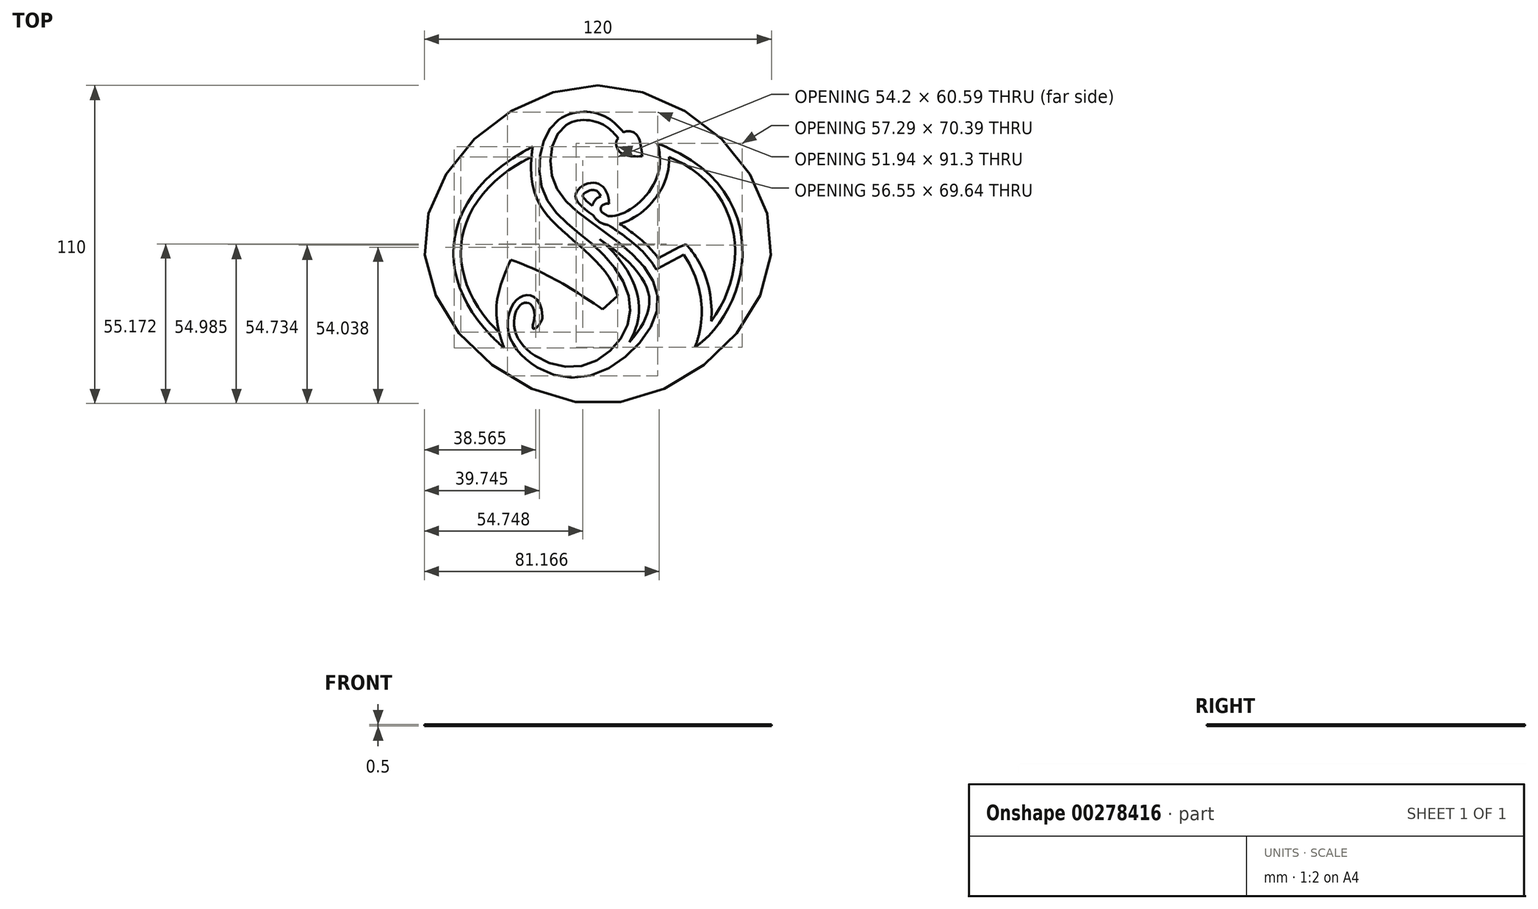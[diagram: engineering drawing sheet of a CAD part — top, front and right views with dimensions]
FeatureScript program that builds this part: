
annotation { "Feature Type Name" : "Feature", "Feature Type Description" : "" }
export const myFeature = defineFeature(function(context is Context, id is Id, definition is map)
    precondition{}
    {
        {
            var Q0;
            Q0=qCreatedBy(makeId("Top.planeOp"),FACE);
            var sketch = newSketch(context, id + "F0", { "sketchPlane" : qUnion([Q0])});
            skPoint(sketch, "E0", {"position": v(0, 45.9) * mm});
            skPoint(sketch, "E1", {"position": v(50, 0) * mm});
            skFitSpline(sketch, "E2", {"points": [v(-32.4, -35.78) * mm, v(-22.5, 33.86) * mm], "startDerivative": vector(-72.76, 61.38) * mm, "endDerivative": vector(106.5, 54.47) * mm});
            skFitSpline(sketch, "E3", {"points": [v(-22.5, 33.86) * mm, v(-11.83, 4.4) * mm, v(6.84, -17.73) * mm], "startDerivative": vector(-15.53, -95.65) * mm, "endDerivative": vector(14.34, -53.92) * mm});
            skFitSpline(sketch, "E4", {"points": [v(-32.4, -35.78) * mm, v(-30.16, -5.24) * mm], "startDerivative": vector(-15.68, 40.02) * mm, "endDerivative": vector(13, 31.32) * mm});
            skFitSpline(sketch, "E5", {"points": [v(-30.16, -5.24) * mm, v(1.65, -22.42) * mm], "startDerivative": vector(35.17, -12.5) * mm, "endDerivative": vector(34.2, -23.48) * mm});
            skLineSegment(sketch, "E6", {"start": v(1.65, -22.42) * mm, "end": v(6.84, -17.73) * mm});
            skFitSpline(sketch, "E7", {"points": [v(20.58, 34.93) * mm, v(33.56, -35.46) * mm], "startDerivative": vector(125.66, -46.66) * mm, "endDerivative": vector(-57.33, -38.36) * mm});
            skFitSpline(sketch, "E8", {"points": [v(33.56, -35.46) * mm, v(29.63, -3.46) * mm], "startDerivative": vector(13.37, 33.93) * mm, "endDerivative": vector(-18.4, 26.9) * mm});
            skFitSpline(sketch, "E9", {"points": [v(20.58, 34.93) * mm, v(2.5, 10.15) * mm, v(3.85, 14.15) * mm], "startDerivative": vector(20.7, -63.95) * mm, "endDerivative": vector(42.66, -0.52) * mm});
            skFitSpline(sketch, "E10", {"points": [v(29.63, -3.46) * mm, v(20.13, -8.6) * mm], "startDerivative": vector(-9.5, -5.15) * mm, "endDerivative": vector(-9.5, -5.15) * mm});
            skFitSpline(sketch, "E11", {"points": [v(3.85, 14.15) * mm, v(-2.2, 21.34) * mm, v(-7.68, 16.17) * mm, v(20.13, -8.6) * mm], "startDerivative": vector(-2.08, 58.94) * mm, "endDerivative": vector(39.46, -73.33) * mm});
            skFitSpline(sketch, "E12", {"points": [v(-19.17, -24.83) * mm, v(-26.46, -18) * mm, v(-30.6, -31.45) * mm, v(-5.87, -45.9) * mm, v(20.63, -21.21) * mm, v(5.08, 2.3) * mm, v(-15.3, 21.72) * mm, v(-11.54, 40.91) * mm, v(2, 41.36) * mm, v(7.04, 36.8) * mm], "startDerivative": vector(-12.75, 250.76) * mm, "endDerivative": vector(40.26, -40.75) * mm});
            skFitSpline(sketch, "E13", {"points": [v(-22.04, -25.78) * mm, v(-25.84, -20.3) * mm, v(-28.42, -30.72) * mm, v(-7.28, -42.28) * mm, v(10.94, -25.14) * mm, v(0.7, -2.29) * mm, v(-18.36, 17) * mm, v(-16.38, 40.34) * mm, v(-4.35, 45.9) * mm, v(4.17, 43.23) * mm, v(8.8, 38.82) * mm], "startDerivative": vector(32.24, 214.47) * mm, "endDerivative": vector(67.48, -74.16) * mm});
            skFitSpline(sketch, "E14", {"points": [v(-22.04, -25.78) * mm, v(-22.22, -29.13) * mm, v(-19.17, -24.83) * mm], "startDerivative": vector(-3.03, -14.05) * mm, "endDerivative": vector(1.13, 14.14) * mm});
            skFitSpline(sketch, "E15", {"points": [v(7.04, 36.8) * mm, v(6.52, 33.67) * mm, v(8.55, 31.33) * mm, v(15.3, 30.52) * mm], "startDerivative": vector(-8.7, -10.3) * mm, "endDerivative": vector(19.55, 1.32) * mm});
            skFitSpline(sketch, "E16", {"points": [v(8.8, 38.82) * mm, v(11.3, 39.15) * mm, v(13.78, 37.37) * mm, v(15.3, 30.52) * mm], "startDerivative": vector(7.23, 3.73) * mm, "endDerivative": vector(1.32, -17.53) * mm});
            skFitSpline(sketch, "E17", {"points": [v(0, 55) * mm, v(60, 0) * mm, v(0, -55) * mm, v(-60, 0) * mm, v(0, 55) * mm]});
            skFitSpline(sketch, "E18.0", {"points": [v(23.43, 35.85) * mm, v(23.93, 34.32) * mm, v(24.55, 31.27) * mm, v(24.48, 26.9) * mm, v(23.54, 22.83) * mm, v(21.92, 19.15) * mm, v(19.8, 15.9) * mm, v(17.3, 13.09) * mm, v(14.57, 10.74) * mm, v(11.72, 8.88) * mm, v(9.32, 7.76) * mm, v(7.42, 7.15) * mm, v(5.99, 6.85) * mm, v(4.56, 6.72) * mm, v(3.36, 6.8) * mm, v(2.4, 7) * mm, v(1.67, 7.23) * mm, v(0.96, 7.55) * mm, v(0.31, 7.96) * mm, v(-0.27, 8.44) * mm, v(-0.96, 9.15) * mm, v(-1.64, 10.2) * mm, v(-2.03, 11.48) * mm, v(-2.07, 12.62) * mm, v(-1.94, 13.52) * mm, v(-1.6, 14.4) * mm, v(-1.07, 15.21) * mm, v(-0.4, 15.9) * mm, v(0.38, 16.4) * mm, v(1.21, 16.77) * mm, v(2.36, 17.09) * mm, v(3.26, 17.16) * mm, v(3.88, 17.15) * mm]});
            skLineSegment(sketch, "E19.0", {"start": v(-0.36, -20.2) * mm, "end": v(3.39, -16.81) * mm});
            skFitSpline(sketch, "E19.1", {"points": [v(-25.47, 34.34) * mm, v(-25.81, 32.25) * mm, v(-26.23, 28.34) * mm, v(-26.14, 23.16) * mm, v(-25.36, 18.58) * mm, v(-23.96, 14.54) * mm, v(-22.02, 11) * mm, v(-19.68, 7.9) * mm, v(-17.07, 5.13) * mm, v(-14.75, 2.98) * mm, v(-12.85, 1.3) * mm, v(-10.91, -0.4) * mm, v(-8.48, -2.5) * mm, v(-5.63, -5.06) * mm, v(-2.95, -7.66) * mm, v(-0.56, -10.3) * mm, v(1.46, -13) * mm, v(3, -15.73) * mm, v(3.7, -17.57) * mm, v(3.94, -18.5) * mm]});
            skFitSpline(sketch, "E19.2", {"points": [v(-30.47, -33.49) * mm, v(-33.36, -31.05) * mm, v(-38.44, -25.87) * mm, v(-43.78, -17.54) * mm, v(-46.75, -8.95) * mm, v(-47.3, -0.33) * mm, v(-45.3, 8.16) * mm, v(-40.58, 16.43) * mm, v(-32.8, 24.26) * mm, v(-25.42, 29) * mm, v(-21.14, 31.19) * mm]});
            skFitSpline(sketch, "E19.3", {"points": [v(-35.2, -36.88) * mm, v(-35.88, -35.12) * mm, v(-37, -31.8) * mm, v(-37.95, -27.21) * mm, v(-38.23, -22.95) * mm, v(-37.91, -18.96) * mm, v(-37.1, -15.18) * mm, v(-35.55, -10.32) * mm, v(-34, -6.7) * mm, v(-32.93, -4.1) * mm]});
            skFitSpline(sketch, "E20.0", {"points": [v(-29.15, -2.42) * mm, v(-26.15, -3.48) * mm, v(-20.5, -5.76) * mm, v(-12.66, -9.72) * mm, v(-4.93, -14.36) * mm, v(0.48, -17.98) * mm, v(3.35, -19.95) * mm]});
            skLineSegment(sketch, "E21", {"start": v(-32.93, -4.1) * mm, "end": v(-31.1, -1.34) * mm});
            skLineSegment(sketch, "E22", {"start": v(-29.15, -2.42) * mm, "end": v(-31.6, -2.08) * mm});
            skPoint(sketch, "E23", {"position": v(-2.05, 12.14) * mm});
            skPoint(sketch, "E24", {"position": v(5.67, 6.84) * mm});
            skPoint(sketch, "E25", {"position": v(1.33, 16.8) * mm});
            skPoint(sketch, "E26", {"position": v(24.33, 31.77) * mm});
            skPoint(sketch, "E27", {"position": v(21.18, 32.56) * mm});
            skPoint(sketch, "E28", {"position": v(1.4, -18.61) * mm});
            skFitSpline(sketch, "E29.0", {"points": [v(19.54, 32.12) * mm, v(24.55, 30.26) * mm, v(32.92, 25.78) * mm, v(41.15, 17.55) * mm, v(45.8, 8.34) * mm, v(47.39, -1.4) * mm, v(46.34, -11.11) * mm, v(43.09, -20.16) * mm, v(38.1, -27.82) * mm, v(34.02, -31.55) * mm, v(31.9, -32.97) * mm]});
            skFitSpline(sketch, "E30.0", {"points": [v(36.36, -36.56) * mm, v(37.57, -33.49) * mm, v(39.08, -27.26) * mm, v(38.9, -18.08) * mm, v(36.56, -9.41) * mm, v(33.76, -4.2) * mm, v(32.1, -1.77) * mm]});
            skFitSpline(sketch, "E31.0", {"points": [v(28.2, -0.82) * mm, v(25.03, -2.54) * mm, v(21.87, -4.26) * mm, v(18.7, -5.97) * mm]});
            skFitSpline(sketch, "E32.0", {"points": [v(1.35, 14.06) * mm, v(1.31, 15.08) * mm, v(1.08, 16.33) * mm, v(0.57, 17.44) * mm, v(0.15, 18.03) * mm, v(-0.29, 18.43) * mm, v(-0.74, 18.68) * mm, v(-1.24, 18.83) * mm, v(-1.73, 18.87) * mm, v(-2.16, 18.83) * mm, v(-2.65, 18.74) * mm, v(-3.3, 18.54) * mm, v(-4.04, 18.16) * mm, v(-4.65, 17.7) * mm, v(-5.06, 17.24) * mm, v(-5.2, 16.95) * mm, v(-5.24, 16.82) * mm, v(-5.25, 16.76) * mm, v(-5.24, 16.73) * mm, v(-5.24, 16.69) * mm, v(-5.21, 16.61) * mm, v(-5.14, 16.45) * mm, v(-4.9, 16.07) * mm, v(-4.34, 15.4) * mm, v(-3.26, 14.43) * mm, v(-1.86, 13.35) * mm, v(-0.18, 12.18) * mm, v(2.35, 10.5) * mm, v(5.93, 8.2) * mm, v(10.51, 5.09) * mm, v(15.04, 1.53) * mm, v(19.18, -2.56) * mm, v(21.42, -5.72) * mm, v(22.34, -7.43) * mm]});
            skLineSegment(sketch, "E33", {"start": v(28.2, -0.82) * mm, "end": v(30.38, 0) * mm});
            skLineSegment(sketch, "E34", {"start": v(30.38, 0) * mm, "end": v(32.1, -1.77) * mm});
            skFitSpline(sketch, "E35.0", {"points": [v(-22.16, -24.98) * mm, v(-22.22, -23.9) * mm, v(-22.47, -22.62) * mm, v(-22.93, -21.57) * mm, v(-23.28, -21.06) * mm, v(-23.59, -20.76) * mm, v(-23.85, -20.6) * mm, v(-24.1, -20.52) * mm, v(-24.37, -20.5) * mm, v(-24.7, -20.53) * mm, v(-25.08, -20.64) * mm, v(-25.48, -20.86) * mm, v(-25.94, -21.2) * mm, v(-26.4, -21.7) * mm, v(-27, -22.52) * mm, v(-27.67, -23.85) * mm, v(-28.17, -25.8) * mm, v(-28.27, -27.6) * mm, v(-28.11, -29.07) * mm, v(-27.87, -30.17) * mm, v(-27.5, -31.27) * mm, v(-27, -32.4) * mm, v(-26.35, -33.53) * mm, v(-25.3, -35.02) * mm, v(-23.67, -36.84) * mm, v(-21.27, -38.83) * mm, v(-18.52, -40.53) * mm, v(-15.49, -41.86) * mm, v(-12.8, -42.6) * mm, v(-10.62, -42.94) * mm, v(-8.95, -43.06) * mm, v(-7.28, -43.03) * mm, v(-5.62, -42.86) * mm, v(-3.93, -42.54) * mm, v(-1.65, -41.9) * mm, v(1.2, -40.77) * mm, v(4.52, -38.9) * mm, v(7.66, -36.61) * mm, v(10.53, -34) * mm, v(13.02, -31.16) * mm, v(15.07, -28.19) * mm, v(16.33, -25.7) * mm, v(17.05, -23.76) * mm, v(17.43, -22.35) * mm, v(17.62, -21.23) * mm, v(17.7, -20.36) * mm, v(17.75, -19.07) * mm, v(17.55, -17.2) * mm, v(16.78, -14.7) * mm, v(15.5, -12.21) * mm, v(13.2, -8.9) * mm, v(9.32, -4.86) * mm, v(4.63, -1.06) * mm, v(0.73, 1.8) * mm, v(-3.21, 4.6) * mm, v(-7.09, 7.4) * mm, v(-10.68, 10.4) * mm, v(-13.16, 12.82) * mm, v(-15, 15.02) * mm, v(-16.28, 16.92) * mm, v(-17.14, 18.42) * mm, v(-17.88, 20.01) * mm, v(-18.48, 21.68) * mm, v(-18.93, 23.39) * mm, v(-19.35, 25.7) * mm, v(-19.55, 28.64) * mm, v(-19.28, 32.13) * mm, v(-18.51, 35.48) * mm, v(-17.47, 38.08) * mm, v(-16.36, 40) * mm, v(-15.4, 41.33) * mm, v(-14.46, 42.34) * mm, v(-13.64, 43.08) * mm, v(-12.76, 43.76) * mm, v(-11.61, 44.47) * mm, v(-9.67, 45.34) * mm, v(-7.16, 45.97) * mm, v(-4.14, 46.11) * mm, v(-1.71, 45.81) * mm, v(0.14, 45.35) * mm, v(1.48, 44.9) * mm, v(2.75, 44.36) * mm, v(3.95, 43.71) * mm, v(5.01, 43) * mm, v(6.27, 42.02) * mm, v(7.28, 41.03) * mm, v(8.08, 40.16) * mm, v(8.58, 39.59) * mm, v(8.96, 39.14) * mm, v(9.13, 38.96) * mm, v(9.17, 38.92) * mm]});
            skFitSpline(sketch, "E36.0", {"points": [v(-19.07, -26.23) * mm, v(-18.96, -25.53) * mm, v(-18.86, -24.2) * mm, v(-19.04, -22.34) * mm, v(-19.57, -20.64) * mm, v(-20.48, -19.15) * mm, v(-21.75, -17.98) * mm, v(-23.3, -17.26) * mm, v(-24.95, -17.04) * mm, v(-26.3, -17.26) * mm, v(-27.3, -17.65) * mm, v(-28.2, -18.16) * mm, v(-29.17, -18.95) * mm, v(-30.09, -20.07) * mm, v(-30.82, -21.31) * mm, v(-31.38, -22.66) * mm, v(-31.92, -24.58) * mm, v(-32.13, -26.66) * mm, v(-31.98, -28.83) * mm, v(-31.72, -30.22) * mm, v(-31.4, -31.32) * mm, v(-31, -32.43) * mm, v(-30.37, -33.75) * mm, v(-29.44, -35.26) * mm, v(-27.99, -37.15) * mm, v(-25.82, -39.3) * mm, v(-22.77, -41.49) * mm, v(-19.37, -43.27) * mm, v(-15.7, -44.59) * mm, v(-12.49, -45.22) * mm, v(-9.87, -45.4) * mm, v(-7.9, -45.38) * mm, v(-5.91, -45.16) * mm, v(-3.99, -44.75) * mm, v(-2.12, -44.17) * mm, v(0.28, -43.2) * mm, v(3.1, -41.62) * mm, v(6.14, -39.25) * mm, v(8.79, -36.5) * mm, v(11, -33.42) * mm, v(12.42, -30.64) * mm, v(13.27, -28.32) * mm, v(13.75, -26.54) * mm, v(14.06, -24.73) * mm, v(14.24, -22.32) * mm, v(14.06, -19.34) * mm, v(13.26, -15.86) * mm, v(11.98, -12.53) * mm, v(10.3, -9.34) * mm, v(8.28, -6.3) * mm, v(5.99, -3.44) * mm, v(3.9, -1.2) * mm, v(2.14, 0.5) * mm, v(0.36, 2.1) * mm, v(-1.89, 4.01) * mm, v(-5.45, 6.89) * mm, v(-8.8, 9.62) * mm, v(-11.66, 12.4) * mm, v(-13.5, 14.54) * mm, v(-14.73, 16.4) * mm, v(-15.43, 17.78) * mm, v(-15.78, 18.6) * mm, v(-16.27, 19.85) * mm, v(-16.84, 21.88) * mm, v(-17.25, 24.77) * mm, v(-17.3, 27.74) * mm, v(-17.02, 30.67) * mm, v(-16.42, 33.44) * mm, v(-15.54, 35.93) * mm, v(-14.7, 37.5) * mm, v(-14.09, 38.4) * mm, v(-13.67, 38.96) * mm, v(-12.9, 39.84) * mm, v(-11.68, 40.87) * mm, v(-10.05, 41.8) * mm, v(-8.3, 42.44) * mm, v(-6.5, 42.82) * mm, v(-4.69, 42.94) * mm, v(-2.98, 42.83) * mm, v(-1.4, 42.53) * mm, v(0.07, 42.06) * mm, v(1.17, 41.55) * mm, v(1.97, 41.1) * mm, v(2.53, 40.73) * mm, v(3.06, 40.34) * mm, v(3.73, 39.79) * mm, v(4.54, 39.02) * mm, v(5.52, 37.97) * mm, v(6.2, 37.2) * mm, v(6.57, 36.8) * mm]});
            skSolve(sketch);
        }
        {
            var Q0;
            Q0=makeQuery(id+"F0.imprint","IMPRINT",FACE,{"disambiguationData":[TD([[makeQuery(id+"F0.imprint","IMPRINT",EDGE,{"derivedFrom":sQuery(id+"F0.wireOp",EDGE,"E2")}),1.0]])]});
            var Q1;
            {var subQ0=sQuery(id+"F0.wireOp",EDGE,"E16");var subQ1=sQuery(id+"F0.wireOp",EDGE,"E13");var subQ2=makeQuery(id+"F0.imprint","INTERSECT",VERTEX,{"derivedFrom":[subQ1,subQ0]});Q1=makeQuery(id+"F0.imprint","IMPRINT",FACE,{"disambiguationData":[TD([[makeQuery(id+"F0.imprint","IMPRINT",EDGE,{"disambiguationData":[TD([[subQ2,1.0]])],"derivedFrom":subQ1}),1.0]])]});}
            extrude(context, id + "F1", {"entities" : qUnion([Q0, Q1]), "depth" : 0.5 * mm});
        }
        {
            var Q0;
            {var subQ10=sQuery(id+"F0.wireOp",EDGE,"E33");Q0=makeQuery(id+"F0.imprint","IMPRINT",FACE,{"disambiguationData":[TD([[makeQuery(id+"F0.imprint","IMPRINT",EDGE,{"derivedFrom":subQ10}),-1.0]])]});}
            var Q1;
            {var subQ1=sQuery(id+"F0.wireOp",EDGE,"E11");var subQ5=sQuery(id+"F0.wireOp",EDGE,"E10");var subQ6=makeQuery(id+"F0.imprint","INTERSECT",VERTEX,{"derivedFrom":[subQ5,subQ1]});Q1=makeQuery(id+"F0.imprint","IMPRINT",FACE,{"disambiguationData":[TD([[makeQuery(id+"F0.imprint","IMPRINT",EDGE,{"disambiguationData":[TD([[subQ6,1.0]])],"derivedFrom":subQ5}),-1.0]])]});}
            var Q2;
            {var subQ0=sQuery(id+"F0.wireOp",EDGE,"E18.0");var subQ1=sQuery(id+"F0.wireOp",EDGE,"E7");var subQ2=makeQuery(id+"F0.imprint","INTERSECT",VERTEX,{"derivedFrom":[subQ1,subQ0]});Q2=makeQuery(id+"F0.imprint","IMPRINT",FACE,{"disambiguationData":[TD([[makeQuery(id+"F0.imprint","IMPRINT",EDGE,{"disambiguationData":[TD([[subQ2,-1.0]])],"derivedFrom":subQ1}),-1.0]])]});}
            var Q3;
            {var subQ0=sQuery(id+"F0.wireOp",EDGE,"E8");var subQ1=sQuery(id+"F0.wireOp",EDGE,"E7");var subQ2=makeQuery(id+"F0.imprint","INTERSECT",VERTEX,{"derivedFrom":[subQ1,subQ0]});Q3=makeQuery(id+"F0.imprint","IMPRINT",FACE,{"disambiguationData":[TD([[makeQuery(id+"F0.imprint","IMPRINT",EDGE,{"disambiguationData":[TD([[subQ2,1.0]])],"derivedFrom":subQ1}),-1.0]])]});}
            var Q4;
            {var subQ4=sQuery(id+"F0.wireOp",EDGE,"E11");var subQ5=sQuery(id+"F0.wireOp",EDGE,"E9");var subQ6=makeQuery(id+"F0.imprint","INTERSECT",VERTEX,{"derivedFrom":[subQ5,subQ4]});Q4=makeQuery(id+"F0.imprint","IMPRINT",FACE,{"disambiguationData":[TD([[makeQuery(id+"F0.imprint","IMPRINT",EDGE,{"disambiguationData":[TD([[subQ6,1.0]])],"derivedFrom":subQ5}),1.0]])]});}
            var Q5;
            {var subQ0=sQuery(id+"F0.wireOp",EDGE,"E9");var subQ1=sQuery(id+"F0.wireOp",EDGE,"E7");var subQ2=makeQuery(id+"F0.imprint","INTERSECT",VERTEX,{"derivedFrom":[subQ1,subQ0]});Q5=makeQuery(id+"F0.imprint","IMPRINT",FACE,{"disambiguationData":[TD([[makeQuery(id+"F0.imprint","IMPRINT",EDGE,{"disambiguationData":[TD([[subQ2,-1.0]])],"derivedFrom":subQ1}),-1.0]])]});}
            var Q6;
            Q6=makeQuery(id+"F0.imprint","IMPRINT",FACE,{"disambiguationData":[TD([[makeQuery(id+"F0.imprint","IMPRINT",EDGE,{"derivedFrom":sQuery(id+"F0.wireOp",EDGE,"E2")}),1.0]])]});
            var Q7;
            Q7=makeQuery(id+"F0.imprint","IMPRINT",FACE,{"disambiguationData":[TD([[makeQuery(id+"F0.imprint","IMPRINT",EDGE,{"derivedFrom":sQuery(id+"F0.wireOp",EDGE,"E12")}),1.0]])]});
            var Q8;
            Q8=makeQuery(id+"F0.imprint","IMPRINT",FACE,{"disambiguationData":[TD([[makeQuery(id+"F0.imprint","IMPRINT",EDGE,{"derivedFrom":sQuery(id+"F0.wireOp",EDGE,"E2")}),-1.0]])]});
            var Q9;
            {var subQ0=sQuery(id+"F0.wireOp",EDGE,"E35.0");var subQ1=sQuery(id+"F0.wireOp",EDGE,"E13");var subQ2=makeQuery(id+"F0.imprint","INTERSECT",VERTEX,{"disambiguationData":[OD(0.0)],"derivedFrom":[subQ1,subQ0]});Q9=makeQuery(id+"F0.imprint","IMPRINT",FACE,{"disambiguationData":[TD([[makeQuery(id+"F0.imprint","IMPRINT",EDGE,{"disambiguationData":[TD([[subQ2,-1.0]])],"derivedFrom":subQ1}),-1.0]])]});}
            var Q10;
            {var subQ0=sQuery(id+"F0.wireOp",EDGE,"E14");Q10=makeQuery(id+"F0.imprint","IMPRINT",FACE,{"disambiguationData":[TD([[makeQuery(id+"F0.imprint","IMPRINT",EDGE,{"derivedFrom":subQ0}),1.0]])]});}
            var Q11;
            {var subQ10=sQuery(id+"F0.wireOp",EDGE,"E15");Q11=makeQuery(id+"F0.imprint","IMPRINT",FACE,{"disambiguationData":[TD([[makeQuery(id+"F0.imprint","IMPRINT",EDGE,{"derivedFrom":subQ10}),1.0]])]});}
            var Q12;
            {var subQ0=sQuery(id+"F0.wireOp",EDGE,"E18.0");var subQ1=sQuery(id+"F0.wireOp",EDGE,"E11");var subQ2=makeQuery(id+"F0.imprint","INTERSECT",VERTEX,{"disambiguationData":[OD(1.0)],"derivedFrom":[subQ1,subQ0]});Q12=makeQuery(id+"F0.imprint","IMPRINT",FACE,{"disambiguationData":[TD([[makeQuery(id+"F0.imprint","IMPRINT",EDGE,{"disambiguationData":[TD([[subQ2,-1.0]])],"derivedFrom":subQ1}),-1.0]])]});}
            var Q13;
            {var subQ0=sQuery(id+"F0.wireOp",EDGE,"E32.0");var subQ1=sQuery(id+"F0.wireOp",EDGE,"E9");var subQ2=makeQuery(id+"F0.imprint","INTERSECT",VERTEX,{"disambiguationData":[OD(0.0)],"derivedFrom":[subQ1,subQ0]});Q13=makeQuery(id+"F0.imprint","IMPRINT",FACE,{"disambiguationData":[TD([[makeQuery(id+"F0.imprint","IMPRINT",EDGE,{"disambiguationData":[TD([[subQ2,-1.0]])],"derivedFrom":subQ1}),-1.0]])]});}
            var Q14;
            {var subQ3=sQuery(id+"F0.wireOp",EDGE,"E32.0");var subQ7=sQuery(id+"F0.wireOp",EDGE,"E9");var subQ8=makeQuery(id+"F0.imprint","INTERSECT",VERTEX,{"disambiguationData":[OD(0.0)],"derivedFrom":[subQ7,subQ3]});Q14=makeQuery(id+"F0.imprint","IMPRINT",FACE,{"disambiguationData":[TD([[makeQuery(id+"F0.imprint","IMPRINT",EDGE,{"disambiguationData":[TD([[subQ8,-1.0]])],"derivedFrom":subQ7}),1.0]])]});}
            var Q15;
            {var subQ0=sQuery(id+"F0.wireOp",EDGE,"E29.0");var subQ1=sQuery(id+"F0.wireOp",EDGE,"E9");var subQ2=makeQuery(id+"F0.imprint","INTERSECT",VERTEX,{"derivedFrom":[subQ1,subQ0]});Q15=makeQuery(id+"F0.imprint","IMPRINT",FACE,{"disambiguationData":[TD([[makeQuery(id+"F0.imprint","IMPRINT",EDGE,{"disambiguationData":[TD([[subQ2,-1.0]])],"derivedFrom":subQ1}),1.0]])]});}
            var Q16;
            {var subQ0=sQuery(id+"F0.wireOp",EDGE,"E18.0");var subQ1=sQuery(id+"F0.wireOp",EDGE,"E11");var subQ2=makeQuery(id+"F0.imprint","INTERSECT",VERTEX,{"disambiguationData":[OD(0.0)],"derivedFrom":[subQ1,subQ0]});Q16=makeQuery(id+"F0.imprint","IMPRINT",FACE,{"disambiguationData":[TD([[makeQuery(id+"F0.imprint","IMPRINT",EDGE,{"disambiguationData":[TD([[subQ2,-1.0]])],"derivedFrom":subQ1}),1.0]])]});}
            var Q17;
            {var subQ0=sQuery(id+"F0.wireOp",EDGE,"E16");var subQ1=sQuery(id+"F0.wireOp",EDGE,"E13");var subQ2=makeQuery(id+"F0.imprint","INTERSECT",VERTEX,{"derivedFrom":[subQ1,subQ0]});Q17=makeQuery(id+"F0.imprint","IMPRINT",FACE,{"disambiguationData":[TD([[makeQuery(id+"F0.imprint","IMPRINT",EDGE,{"disambiguationData":[TD([[subQ2,1.0]])],"derivedFrom":subQ1}),1.0]])]});}
            extrude(context, id + "F2", {"entities" : qUnion([Q0, Q1, Q2, Q3, Q4, Q5, Q6, Q7, Q8, Q9, Q10, Q11, Q12, Q13, Q14, Q15, Q16, Q17]), "depth" : 0.4 * mm});
        }
    });
